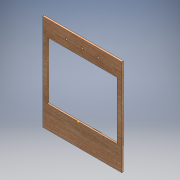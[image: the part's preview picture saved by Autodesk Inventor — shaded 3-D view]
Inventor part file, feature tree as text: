
AUTODESK INVENTOR PART (.ipt)
format: ipt  version: 2016 (Build 200138000, 138)  size: 201,216 bytes
history: native  units: mm
features: sketch x9, hole x5, extrude x3
ambient origin geometry x8: Origin, YZ Plane, XZ Plane, XY Plane, X Axis, Y Axis, Z Axis, Center Point
bodies: Solid1 (feature_tree)
feature tree (17):
  extrude  "Extrusion1"  Depth=100.0mm
  extrude  "Extrusion2"  Depth=35.0mm
  hole  "Hole1"  [1 undecoded]
  sketch  "Sketch4"  dims[d13=62.0mm d14=0.0mm d15=4.25mm]
  hole  "Hole2"  [1 undecoded]
  hole  "Hole3"  [1 undecoded]
  hole  "Hole4"  [1 undecoded]
  extrude  "Extrusion3"  Depth=20.0mm
  hole  "Hole5"  [1 undecoded]
  sketch  "Sketch1"  dims[d0=350.0mm d1=100.0mm]
  sketch  "Sketch2"  dims[d8=6.35mm d9=0.0mm d10=35.0mm]
  sketch  "Sketch3"  dims[d11=40.0mm d12=157.5mm]
  sketch  "Sketch5"  dims[d16=6.0mm d17=4.25mm]
  sketch  "Sketch6"  dims[d18=6.0mm d19=4.25mm]
  sketch  "Sketch7"  dims[d20=6.0mm]
  sketch  "Sketch8"  dims[d21=4.25mm d22=6.0mm d23=4.0mm d24=2.0mm d25=90.0deg d26=8.0mm d27=20.594885mm d28=20.0mm]
  sketch  "Sketch9"  dims[d29=3.0mm d30=3.0mm d31=6.0mm d32=6.0mm d33=6.0mm d34=6.0mm d35=3.0mm d36=6.0mm d37=4.0mm d38=2.0mm d39=90.0deg d40=2.0mm d41=20.594885mm d42=20.0mm d43=3.0mm d44=6.0mm d45=6.0mm d46=3.0mm d47=6.0mm d48=6.0mm d49=3.0mm d50=6.0mm d51=4.0mm d52=2.0mm d53=90.0deg d54=2.0mm d55=20.594885mm d56=3.0mm d57=3.0mm d58=3.0mm d59=6.0mm d60=4.0mm d61=2.0mm d62=90.0deg d63=2.0mm d64=20.594885mm d65=20.0mm d66=425.0mm d71=7.5mm d72=0.0mm d73=7.0mm d74=10.0mm d75=10.0mm d76=10.0mm d77=70.0mm d78=70.0mm d79=10.0mm d80=6.0mm d81=4.0mm d82=2.0mm d83=90.0deg d84=8.0mm d85=20.594885mm]
note: 5 required parameter values undecoded (feature->parameter linkage not recoverable at this tier; creation-order binding heuristic only, values carry confidence <= 0.55)
